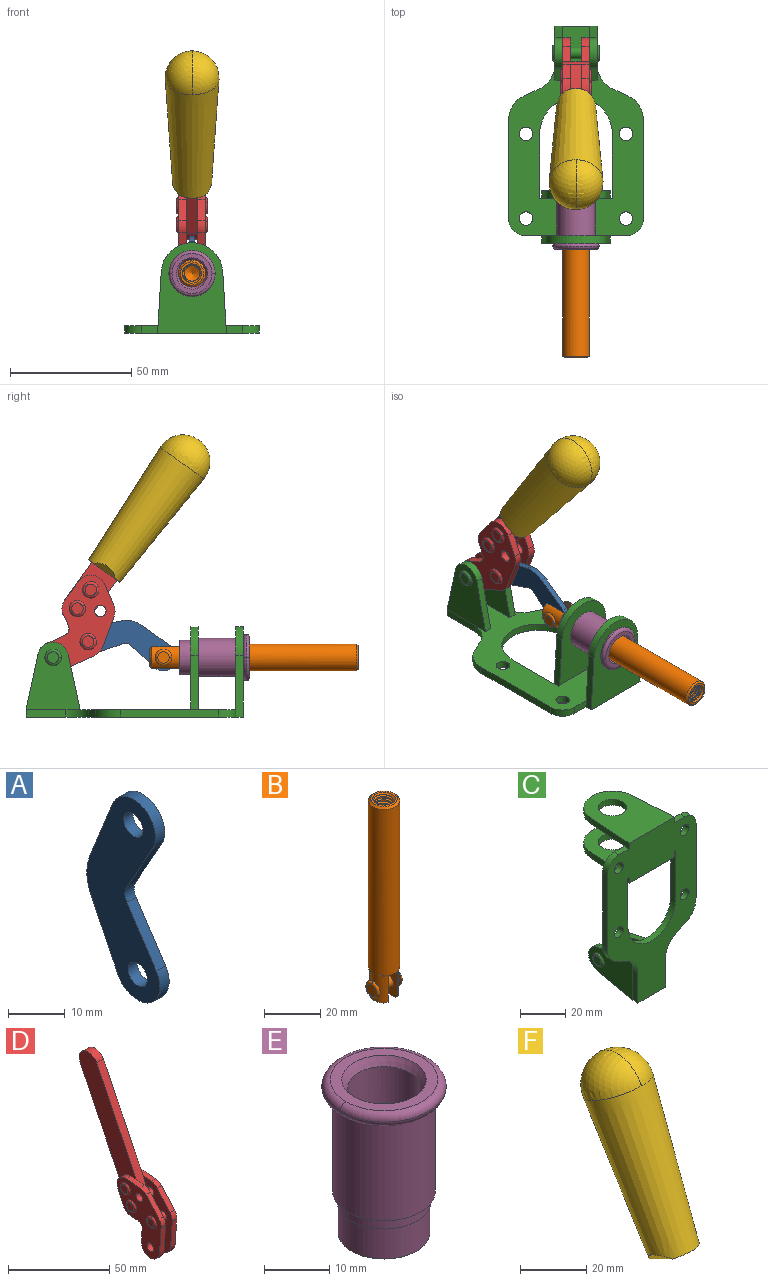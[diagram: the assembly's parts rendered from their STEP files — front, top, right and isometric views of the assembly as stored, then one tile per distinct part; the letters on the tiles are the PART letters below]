
ASSEMBLY  parts=6 mates=7
PART A: 12 faces, bbox 2.3x18.2x42.8 mm
  f0: cylinder r=2.4mm len=4.8mm, axis (1,0,0), area 34.9mm2, adj f4,f11
  f1: cylinder r=10.41mm len=8.47mm, axis (1,0,0), area 20.2mm2, adj f4,f9,f10,f11
  f2: cylinder r=3.05mm len=3.16mm, axis (1,0,0), area 7.7mm2, adj f4,f6,f7,f11
  f3: cylinder r=2.4mm len=4.8mm, axis (1,0,0), area 34.9mm2, adj f4,f11
  f4: plane 42.81x18.23mm, normal (-1,0,0), area 414.1mm2, adj f0,f1,f2,f3,f5,f6,f7,f8
  f5: cylinder r=5.54mm len=10.67mm, axis (1,0,0), area 41.8mm2, adj f4,f6,f10,f11
  f6: plane 11.66x6.53mm, normal (0,-0.87,-0.49), area 30.9mm2, adj f2,f4,f5,f11
  f7: plane 11.17x7.33mm, normal (0,-0.84,0.55), area 30.9mm2, adj f2,f4,f8,f11
  f8: cylinder r=5.54mm len=10.51mm, axis (1,0,0), area 41.8mm2, adj f4,f7,f9,f11
  f9: plane 13.67x6.67mm, normal (0,0.9,-0.44), area 35.1mm2, adj f1,f4,f8,f11
  f10: plane 14.1x5.7mm, normal (0,0.93,0.37), area 35.1mm2, adj f1,f4,f5,f11
  f11: plane 42.81x18.23mm, normal (1,0,0), area 414.1mm2, adj f0,f1,f2,f3,f5,f6,f7,f8
PART B: 48 faces, bbox 12.6x11.1x86.1 mm
  f0: torus R=2.41mm, axis (-1,0,0), area 15mm2, adj f30,f32,f34
  f1: torus R=2.41mm, axis (-1,0,0), area 15mm2, adj f29,f31,f33
  f2: cylinder r=5.54mm len=72.39mm, axis (0,0,1), area 2518.5mm2, adj f3,f4,f42,f43
  f3: cone r=5.54mm half-angle=45deg, axis (0,0,1), area 7.6mm2, adj f2,f5,f41
  f4: cone r=5.54mm half-angle=45deg, axis (0,0,-1), area 34.9mm2, adj f2,f39
  f5: cylinder r=5.08mm len=11.48mm, axis (0,0,1), area 108.3mm2, adj f3,f7,f8,f41
  f6: cylinder r=2.41mm len=4.83mm, axis (-1,0,0), area 71.2mm2, adj f40,f41
  f7: cylinder r=2.41mm len=4.83mm, axis (-1,0,0), area 7.6mm2, adj f5,f34
  f8: cone r=5.08mm half-angle=45deg, axis (0,0,1), area 10.6mm2, adj f5,f37,f41
  f9: cone r=3.98mm half-angle=45deg, axis (0,0,1), area 17.6mm2, adj f27,f39,f45,f46,f47
  f10: cylinder r=2.41mm len=4.83mm, axis (-1,0,0), area 7.6mm2, adj f33,f38
  f11: cylinder r=3.2mm len=6.4mm, axis (0,0,1), area 78.4mm2, adj f12,f28,f44,f45,f47
  f12: cylinder r=3.2mm len=6.4mm, axis (0,0,1), area 10.5mm2, adj f11,f13,f45,f47
  f13: cylinder r=3.2mm len=6.4mm, axis (0,0,1), area 10.5mm2, adj f12,f14,f45,f47
  f14: cylinder r=3.2mm len=6.4mm, axis (0,0,1), area 10.5mm2, adj f13,f15,f45,f47
  f15: cylinder r=3.2mm len=6.4mm, axis (0,0,1), area 10.5mm2, adj f14,f16,f45,f47
  f16: cylinder r=3.2mm len=6.4mm, axis (0,0,1), area 10.5mm2, adj f15,f17,f45,f47
  f17: cylinder r=3.2mm len=6.4mm, axis (0,0,1), area 10.5mm2, adj f16,f18,f45,f47
  f18: cylinder r=3.2mm len=6.4mm, axis (0,0,1), area 10.5mm2, adj f17,f19,f45,f47
  f19: cylinder r=3.2mm len=6.4mm, axis (0,0,1), area 10.5mm2, adj f18,f20,f45,f47
  f20: cylinder r=3.2mm len=6.4mm, axis (0,0,1), area 10.5mm2, adj f19,f21,f45,f47
  f21: cylinder r=3.2mm len=6.4mm, axis (0,0,1), area 10.5mm2, adj f20,f22,f45,f47
  f22: cylinder r=3.2mm len=6.4mm, axis (0,0,1), area 10.5mm2, adj f21,f23,f45,f47
  f23: cylinder r=3.2mm len=6.4mm, axis (0,0,1), area 10.5mm2, adj f22,f24,f45,f47
  f24: cylinder r=3.2mm len=6.4mm, axis (0,0,1), area 10.5mm2, adj f23,f25,f45,f47
  f25: cylinder r=3.2mm len=6.4mm, axis (0,0,1), area 10.5mm2, adj f24,f26,f45,f47
  f26: cylinder r=3.2mm len=6.4mm, axis (0,0,1), area 10.5mm2, adj f25,f27,f45,f47
  f27: cylinder r=3.2mm len=6.4mm, axis (0,0,1), area 7.4mm2, adj f9,f26,f45,f47
  f28: cone r=3.2mm half-angle=60deg, axis (0,0,1), area 37.2mm2, adj f11
  f29: plane 4.83x4.83mm, normal (-1,0,0), area 18.3mm2, adj f1,f31
  f30: plane 4.83x4.83mm, normal (1,0,0), area 18.3mm2, adj f0,f32
  f31: torus R=2.41mm, axis (-1,0,0), area 15mm2, adj f1,f29,f33
  f32: torus R=2.41mm, axis (-1,0,0), area 15mm2, adj f0,f30,f34
  f33: plane 6.83x6.83mm, normal (1,0,0), area 18.3mm2, adj f1,f10,f31
  f34: plane 6.83x6.83mm, normal (-1,0,0), area 18.3mm2, adj f0,f7,f32
  f35: cone r=5.08mm half-angle=45deg, axis (0,0,1), area 10.6mm2, adj f36,f38,f40
  f36: plane 7.25x1.97mm, normal (0,0,-1), area 10mm2, adj f35,f40
  f37: plane 7.25x1.97mm, normal (0,0,-1), area 10mm2, adj f8,f41
  f38: cylinder r=5.08mm len=11.48mm, axis (0,0,1), area 108.3mm2, adj f10,f35,f40,f42
  f39: plane 9.55x9.55mm, normal (0,0,1), area 22mm2, adj f4,f9
  f40: plane 12.76x10.09mm, normal (1,0,0), area 95.7mm2, adj f6,f35,f36,f38,f42,f43
  f41: plane 12.76x10.09mm, normal (-1,0,0), area 95.7mm2, adj f3,f5,f6,f8,f37,f43
  f42: cone r=5.54mm half-angle=45deg, axis (0,0,1), area 7.6mm2, adj f2,f38,f40
  f43: plane 11.07x4.7mm, normal (0,0,-1), area 50.4mm2, adj f2,f40,f41
  f44: plane 0.89x0.62mm, normal (-1,0,0), area 0.3mm2, adj f11,f45,f46,f47
  f45: bspline ~24.8x7.63mm, area 266.6mm2, adj f9,f11,f12,f13,f14,f15,f16,f17
  f46: bspline ~24.87x7.63mm, area 73.6mm2, adj f9,f44,f45,f47
  f47: bspline ~24.98x7.63mm, area 272.5mm2, adj f9,f11,f12,f13,f14,f15,f16,f17
PART C: 55 faces, bbox 55.7x37.4x89.8 mm
  f0: torus R=2.41mm, axis (-1,0,0), area 15mm2, adj f11,f15,f25
  f1: torus R=2.41mm, axis (-1,0,0), area 15mm2, adj f10,f12,f22
  f2: cylinder r=2.78mm len=5.56mm, axis (0,-1,0), area 54.2mm2, adj f30,f54
  f3: cylinder r=14.99mm len=29.97mm, axis (0,-1,0), area 145.9mm2, adj f30,f49,f53,f54
  f4: cylinder r=2.78mm len=5.56mm, axis (0,-1,0), area 54.2mm2, adj f30,f54
  f5: cylinder r=2.78mm len=5.56mm, axis (0,-1,0), area 54.2mm2, adj f30,f54
  f6: cylinder r=2.78mm len=5.56mm, axis (0,-1,0), area 54.2mm2, adj f30,f54
  f7: cylinder r=6.35mm len=12.7mm, axis (0,0,1), area 123.6mm2, adj f27,f51
  f8: cylinder r=6.35mm len=12.7mm, axis (0,0,-1), area 124.7mm2, adj f21,f35
  f9: cylinder r=2.41mm len=11.18mm, axis (-1,0,0), area 169.4mm2, adj f16,f19
  f10: plane 4.83x4.83mm, normal (1,0,0), area 18.3mm2, adj f1,f12
  f11: plane 4.83x4.83mm, normal (-1,0,0), area 18.3mm2, adj f0,f15
  f12: torus R=2.41mm, axis (-1,0,0), area 15mm2, adj f1,f10,f22
  f13: cylinder r=6.35mm len=12.41mm, axis (1,0,0), area 53.4mm2, adj f18,f19,f22,f23
  f14: cylinder r=6.35mm len=12.41mm, axis (-1,0,0), area 53.4mm2, adj f16,f17,f24,f25
  f15: torus R=2.41mm, axis (-1,0,0), area 15mm2, adj f0,f11,f25
  f16: plane 27.86x22.35mm, normal (1,0,0), area 425.4mm2, adj f9,f14,f17,f24,f30
  f17: plane 22.86x4.97mm, normal (0,0.21,0.98), area 72.5mm2, adj f14,f16,f25,f30
  f18: plane 22.86x4.97mm, normal (0,0.21,0.98), area 72.5mm2, adj f13,f19,f22,f30
  f19: plane 27.86x22.35mm, normal (-1,0,0), area 425.4mm2, adj f9,f13,f18,f23,f30
  f20: cylinder r=12.7mm len=25.35mm, axis (0,0,-1), area 119.8mm2, adj f21,f34,f35,f36
  f21: plane 34.21x28.07mm, normal (0,0,-1), area 702.4mm2, adj f8,f20,f30,f34,f36
  f22: plane 27.96x22.45mm, normal (1,0,0), area 407.2mm2, adj f1,f12,f13,f18,f23,f30,f42,f43
  f23: plane 22.86x4.97mm, normal (0,0.21,-0.98), area 72.5mm2, adj f13,f19,f22,f44
  f24: plane 22.86x4.97mm, normal (0,0.21,-0.98), area 72.5mm2, adj f14,f16,f25,f44
  f25: plane 27.86x22.35mm, normal (-1,0,0), area 407.1mm2, adj f0,f14,f15,f17,f24,f30,f45,f46
  f26: plane 3.1x0.95mm, normal (0,0,-1), area 2.7mm2, adj f30,f49,f50,f54
  f27: plane 34.21x28.07mm, normal (0,0,1), area 702.4mm2, adj f7,f28,f30,f50,f52
  f28: cylinder r=12.7mm len=25.35mm, axis (0,0,1), area 118.8mm2, adj f27,f50,f51,f52
  f29: plane 3.1x0.95mm, normal (0,0,-1), area 2.7mm2, adj f30,f52,f53,f54
  f30: plane 86.54x55.63mm, normal (0,1,0), area 2362.9mm2, adj f2,f3,f4,f5,f6,f16,f17,f18
  f31: plane 40.56x3.1mm, normal (-1,0,0), area 125.7mm2, adj f30,f32,f48,f54
  f32: cylinder r=7.11mm len=7.11mm, axis (0,-1,0), area 34.6mm2, adj f30,f31,f33,f54
  f33: plane 6.67x3.1mm, normal (0,0,1), area 20.4mm2, adj f30,f32,f34,f54
  f34: plane 25.39x3.13mm, normal (-1,0.06,0), area 79.5mm2, adj f20,f21,f33,f35,f54
  f35: plane 37.31x28.45mm, normal (0,0,1), area 789.9mm2, adj f8,f20,f34,f36,f54
  f36: plane 25.39x3.13mm, normal (1,0.06,0), area 79.5mm2, adj f20,f21,f35,f37,f54
  f37: plane 6.67x3.1mm, normal (0,0,1), area 20.4mm2, adj f30,f36,f38,f54
  f38: cylinder r=7.11mm len=7.11mm, axis (0,-1,0), area 34.6mm2, adj f30,f37,f39,f54
  f39: plane 40.56x3.1mm, normal (1,0,0), area 125.7mm2, adj f30,f38,f40,f54
  f40: cylinder r=11.18mm len=10.16mm, axis (0,-1,0), area 39.5mm2, adj f30,f39,f41,f54
  f41: plane 6.09x3.1mm, normal (0.42,0,-0.91), area 20.8mm2, adj f30,f40,f42,f54
  f42: cylinder r=11.18mm len=9.41mm, axis (0,-1,0), area 37.2mm2, adj f22,f30,f41,f43,f54
  f43: plane 16.5x3.1mm, normal (1,0,0), area 51.1mm2, adj f22,f42,f44,f54
  f44: plane 17.37x3.1mm, normal (0,0,-1), area 53.8mm2, adj f23,f24,f30,f43,f45,f54
  f45: plane 16.5x3.1mm, normal (-1,0,0), area 51.1mm2, adj f25,f44,f46,f54
  f46: cylinder r=11.18mm len=9.41mm, axis (0,-1,0), area 37.2mm2, adj f25,f30,f45,f47,f54
  f47: plane 6.09x3.1mm, normal (-0.42,0,-0.91), area 20.8mm2, adj f30,f46,f48,f54
  f48: cylinder r=11.18mm len=10.16mm, axis (0,-1,0), area 39.5mm2, adj f30,f31,f47,f54
  f49: plane 26.54x3.1mm, normal (-1,0,0), area 82.3mm2, adj f3,f26,f30,f54
  f50: plane 25.39x3.1mm, normal (1,0.06,0), area 78.8mm2, adj f26,f27,f28,f51,f54
  f51: plane 37.31x28.45mm, normal (0,0,-1), area 789.9mm2, adj f7,f28,f50,f52,f54
  f52: plane 25.39x3.1mm, normal (-1,0.06,0), area 78.8mm2, adj f27,f28,f29,f51,f54
  f53: plane 26.54x3.1mm, normal (1,0,0), area 82.3mm2, adj f3,f29,f30,f54
  f54: plane 89.66x55.63mm, normal (0,-1,0), area 2678.5mm2, adj f2,f3,f4,f5,f6,f26,f29,f31
PART D: 59 faces, bbox 12.9x60.2x99.6 mm
  f0: torus R=2.39mm, axis (-1,0,0), area 14.9mm2, adj f20,f43,f51
  f1: torus R=2.39mm, axis (-1,0,0), area 14.9mm2, adj f19,f42,f51
  f2: torus R=2.39mm, axis (-1,0,0), area 14.9mm2, adj f18,f35,f51
  f3: torus R=2.39mm, axis (-1,0,0), area 14.9mm2, adj f14,f17,f23
  f4: torus R=2.39mm, axis (-1,0,0), area 14.9mm2, adj f13,f16,f23
  f5: torus R=2.39mm, axis (-1,0,0), area 14.9mm2, adj f12,f15,f23
  f6: cylinder r=2.39mm len=4.78mm, axis (1,0,0), area 46.5mm2, adj f48,f50,f51
  f7: cylinder r=2.39mm len=4.78mm, axis (1,0,0), area 46.5mm2, adj f50,f51
  f8: cylinder r=6.35mm len=12.68mm, axis (1,0,0), area 61.8mm2, adj f38,f39,f50,f51
  f9: cylinder r=2.39mm len=4.78mm, axis (-1,0,0), area 70.5mm2, adj f46,f50
  f10: cylinder r=2.39mm len=4.78mm, axis (-1,0,0), area 46.5mm2, adj f23,f45,f46
  f11: cylinder r=2.39mm len=4.78mm, axis (-1,0,0), area 46.5mm2, adj f23,f46
  f12: plane 4.78x4.78mm, normal (1,0,0), area 17.9mm2, adj f5,f15
  f13: plane 4.78x4.78mm, normal (1,0,0), area 17.9mm2, adj f4,f16
  f14: plane 4.78x4.78mm, normal (1,0,0), area 17.9mm2, adj f3,f17
  f15: torus R=2.39mm, axis (-1,0,0), area 14.9mm2, adj f5,f12,f23
  f16: torus R=2.39mm, axis (-1,0,0), area 14.9mm2, adj f4,f13,f23
  f17: torus R=2.39mm, axis (-1,0,0), area 14.9mm2, adj f3,f14,f23
  f18: plane 4.78x4.78mm, normal (-1,0,0), area 17.9mm2, adj f2,f35
  f19: plane 4.78x4.78mm, normal (-1,0,0), area 17.9mm2, adj f1,f42
  f20: plane 4.78x4.78mm, normal (-1,0,0), area 17.9mm2, adj f0,f43
  f21: plane 2.26x0.2mm, normal (1,0,0), area 0.2mm2, adj f31,f44
  f22: plane 2.26x0.2mm, normal (-1,0,0), area 0.2mm2, adj f41,f44
  f23: plane 39.37x30.77mm, normal (1,0,0), area 565.5mm2, adj f3,f4,f5,f10,f11,f15,f16,f17
  f24: cylinder r=6.1mm len=4.15mm, axis (-1,0,0), area 14.7mm2, adj f23,f25,f32,f46
  f25: plane 10.25x9.01mm, normal (0,-0.75,0.66), area 42.3mm2, adj f23,f24,f26,f46
  f26: cylinder r=6.35mm len=4.64mm, axis (-1,0,0), area 15.6mm2, adj f23,f25,f27,f46
  f27: plane 15.84x3.1mm, normal (0,-1,-0.07), area 49.2mm2, adj f23,f26,f28,f46
  f28: cylinder r=6.35mm len=12.68mm, axis (-1,0,0), area 61.8mm2, adj f23,f27,f29,f46
  f29: plane 8.11x3.1mm, normal (0,1,0.07), area 25.2mm2, adj f23,f28,f30,f46
  f30: cylinder r=3.05mm len=3.25mm, axis (-1,0,0), area 14.8mm2, adj f23,f29,f31,f46
  f31: plane 5.99x3.1mm, normal (0,0.07,-1), area 18.6mm2, adj f21,f23,f30,f44,f46
  f32: plane 9.5x3.1mm, normal (0,-0.07,1), area 29.5mm2, adj f23,f24,f33,f46,f47
  f33: cylinder r=6.1mm len=8.63mm, axis (-1,0,0), area 39.1mm2, adj f23,f32,f34,f47
  f34: plane 8.65x3.96mm, normal (0,0.91,-0.42), area 29.5mm2, adj f23,f33,f44,f47
  f35: torus R=2.39mm, axis (-1,0,0), area 14.9mm2, adj f2,f18,f51
  f36: plane 10.25x9.01mm, normal (0,-0.75,0.66), area 42.3mm2, adj f37,f49,f50,f51
  f37: cylinder r=6.35mm len=4.64mm, axis (1,0,0), area 15.6mm2, adj f36,f38,f50,f51
  f38: plane 15.84x3.1mm, normal (0,-1,-0.07), area 49.2mm2, adj f8,f37,f50,f51
  f39: plane 8.11x3.1mm, normal (0,1,0.07), area 25.2mm2, adj f8,f40,f50,f51
  f40: cylinder r=3.05mm len=3.25mm, axis (1,0,0), area 14.8mm2, adj f39,f41,f50,f51
  f41: plane 5.99x3.1mm, normal (0,0.07,-1), area 18.6mm2, adj f22,f40,f44,f50,f51
  f42: torus R=2.39mm, axis (-1,0,0), area 14.9mm2, adj f1,f19,f51
  f43: torus R=2.39mm, axis (-1,0,0), area 14.9mm2, adj f0,f20,f51
  f44: cylinder r=6.35mm len=12.12mm, axis (-1,0,0), area 128.9mm2, adj f21,f22,f23,f31,f34,f41,f46,f47
  f45: plane 2.65x1.35mm, normal (1,0,0), area 1mm2, adj f10,f55
  f46: plane 39.08x20.42mm, normal (-1,0,0), area 412.5mm2, adj f9,f10,f11,f24,f25,f26,f27,f28
  f47: plane 77.62x39.82mm, normal (1,0,0), area 850mm2, adj f32,f33,f34,f44,f53,f54,f55
  f48: plane 2.65x1.35mm, normal (-1,0,0), area 1mm2, adj f6,f55
  f49: cylinder r=6.1mm len=4.15mm, axis (1,0,0), area 14.7mm2, adj f36,f50,f51,f56
  f50: plane 39.08x20.42mm, normal (1,0,0), area 412.5mm2, adj f6,f7,f8,f9,f36,f37,f38,f39
  f51: plane 39.37x30.77mm, normal (-1,0,0), area 565.5mm2, adj f0,f1,f2,f6,f7,f8,f35,f36
  f52: plane 8.65x3.96mm, normal (0,0.91,-0.42), area 29.5mm2, adj f44,f51,f57,f58
  f53: plane 68.49x33.4mm, normal (0,0.9,-0.44), area 358.1mm2, adj f44,f47,f54,f58
  f54: cylinder r=6.35mm len=12.06mm, axis (1,0,0), area 93.7mm2, adj f47,f53,f55,f58
  f55: plane 68.49x33.4mm, normal (0,-0.9,0.44), area 358.1mm2, adj f44,f45,f46,f47,f48,f50,f54,f58
  f56: plane 9.5x3.1mm, normal (0,-0.07,1), area 29.5mm2, adj f49,f50,f51,f57,f58
  f57: cylinder r=6.1mm len=8.63mm, axis (1,0,0), area 39.1mm2, adj f51,f52,f56,f58
  f58: plane 77.62x39.82mm, normal (-1,0,0), area 850mm2, adj f44,f52,f53,f54,f55,f56,f57
PART E: 15 faces, bbox 20.6x20.6x28.7 mm
  f0: torus R=8.26mm, axis (0,0,1), area 56.8mm2, adj f1,f10,f12
  f1: torus R=8.26mm, axis (0,0,1), area 56.8mm2, adj f0,f6,f13
  f2: cylinder r=5.59mm len=25.91mm, axis (0,0,1), area 909.6mm2, adj f3,f4
  f3: cone r=6.86mm half-angle=45deg, axis (0,0,-1), area 70.2mm2, adj f2,f14
  f4: cone r=6.47mm half-angle=30deg, axis (0,0,1), area 66.7mm2, adj f2,f13
  f5: cylinder r=7.04mm len=14.07mm, axis (0,0,1), area 252.6mm2, adj f11,f14
  f6: torus R=8.26mm, axis (0,0,1), area 56.8mm2, adj f1,f12,f13
  f7: cylinder r=7.16mm len=14.33mm, axis (0,0,1), area 91.5mm2, adj f9,f11
  f8: cylinder r=7.86mm len=18.42mm, axis (0,0,1), area 909.6mm2, adj f9,f10
  f9: plane 15.72x15.72mm, normal (0,0,-1), area 33mm2, adj f7,f8
  f10: plane 16.51x16.51mm, normal (0,0,-1), area 19.9mm2, adj f0,f8,f12
  f11: plane 14.33x14.33mm, normal (0,0,-1), area 5.7mm2, adj f5,f7
  f12: torus R=8.26mm, axis (0,0,1), area 56.8mm2, adj f0,f6,f10
  f13: plane 16.51x16.51mm, normal (0,0,1), area 82.7mm2, adj f1,f4,f6
  f14: plane 14.07x14.07mm, normal (0,0,-1), area 7.8mm2, adj f3,f5
PART F: 11 faces, bbox 22.3x42.6x64.5 mm
  f0: sphere r=11.13mm, area 411.4mm2, adj f1,f8
  f1: cone r=11.11mm half-angle=3.3deg, axis (0,0.44,0.9), area 3251.8mm2, adj f0,f7,f8,f9,f10
  f2: cylinder r=6.16mm len=11.7mm, axis (1,0,0), area 89.5mm2, adj f3,f4,f5,f6
  f3: plane 60.23x36.75mm, normal (-1,0,0), area 763.6mm2, adj f2,f4,f6,f10
  f4: plane 51.37x25.05mm, normal (0,0.9,-0.44), area 264.2mm2, adj f2,f3,f5,f10
  f5: plane 60.23x36.75mm, normal (1,0,0), area 763.6mm2, adj f2,f4,f6,f10
  f6: plane 51.37x25.05mm, normal (0,-0.9,0.44), area 264.2mm2, adj f2,f3,f5,f10
  f7: plane 9.95x5.95mm, normal (0.71,-0.31,-0.64), area 25.8mm2, adj f1,f10
  f8: sphere r=11.13mm, area 411.4mm2, adj f0,f1
  f9: plane 9.95x5.95mm, normal (-0.71,-0.31,-0.64), area 25.8mm2, adj f1,f10
  f10: plane 14.27x11.38mm, normal (0,-0.44,-0.9), area 106.7mm2, adj f1,f3,f4,f5,f6,f7,f9
PLACE A rot(axis=(1,0,0),103.9deg) t=(0,8.7,4.42)mm
PLACE B rot(axis=(1,0,0),90deg) t=(0,3.25,0)mm
PLACE C rot(axis=(1,0,0),90deg) t=(0,1.23,0)mm fixed
PLACE D rot(axis=(1,0,0),61.7deg) t=(0,-6.6,18.13)mm
PLACE E rot(axis=(1,0,0),90deg) t=(0,1.23,0)mm
PLACE F rot(axis=(1,0,0),61.7deg) t=(0.04,-6.6,18.13)mm
MATE revolute A.f3 <-> D.f4  axis (1,0,0) through (0,18.85,31.14)mm
MATE fastened C.f7 <-> E.f0  axis (0,-1,0) through (0,-45.16,24.61)mm
MATE fastened F.f2 <-> D.f54  axis (-1,0,0) through (2.35,-21.2,106.64)mm
MATE revolute D.f7 <-> C.f0  axis (1,0,0) through (0,33.32,24.61)mm
MATE revolute A.f3 <-> D.f4  axis (1,0,0) through (0,18.85,31.14)mm
MATE slider C.f7 <-> B.f2  axis (0,-1,0) through (0,-45.16,24.61)mm
MATE revolute B.f6 <-> A.f5  axis (-1,0,0) through (0,-12.22,24.61)mm
